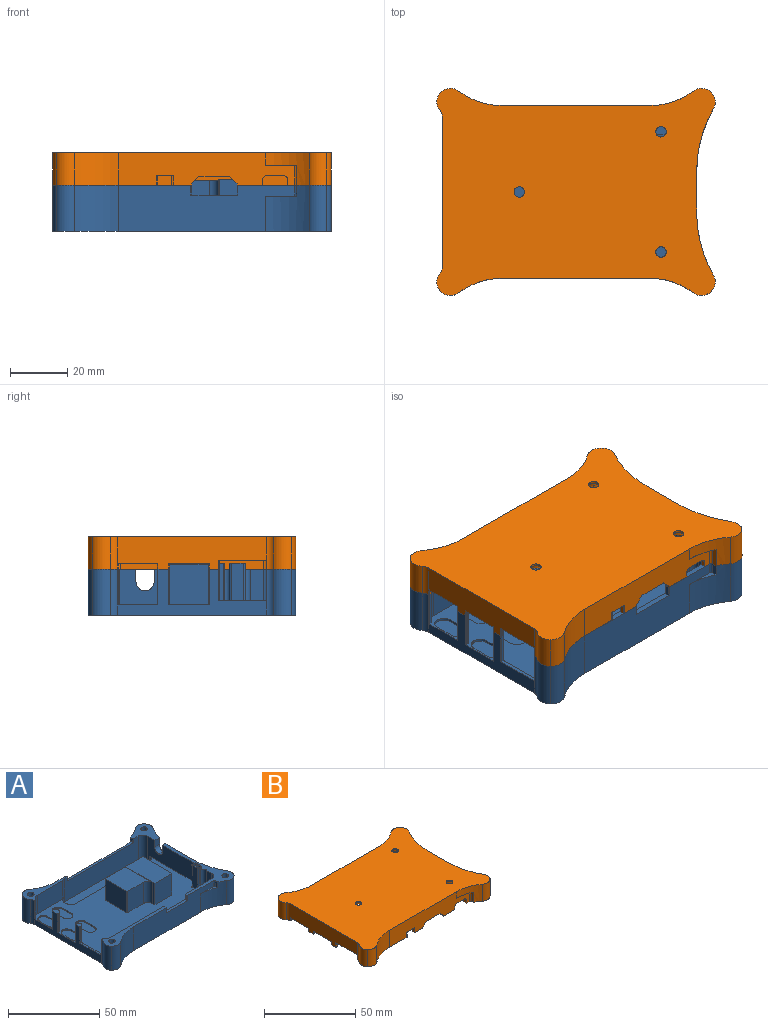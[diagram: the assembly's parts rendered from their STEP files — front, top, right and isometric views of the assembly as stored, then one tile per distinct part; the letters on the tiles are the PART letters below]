
ASSEMBLY  parts=2 mates=1
PART A: 184 faces, bbox 97.3x72.4x18.3 mm
  f0: plane 87x56.52mm, normal (0,0,1), area 3437.9mm2, adj f1,f10,f11,f12,f13,f14,f15,f16
  f1: plane 13.85x1.52mm, normal (1,0,0), area 21.1mm2, adj f0,f59,f88,f141,f172
  f2: plane 20.54x16.18mm, normal (0,0,1), area 276.9mm2, adj f108,f109,f110,f111,f112,f113,f114,f159
  f3: cylinder r=1.83mm len=13.48mm, axis (0,0,-1), area 154.9mm2, adj f62,f157
  f4: cylinder r=1.09mm len=18.29mm, axis (0,0,-1), area 125.5mm2, adj f5,f6
  f5: plane 5.71x3.11mm, normal (0,0,1), area 8.8mm2, adj f4,f7,f8,f9,f10,f11,f12,f13
  f6: plane 97.31x72.42mm, normal (0,0,-1), area 5503.1mm2, adj f4,f19,f20,f21,f22,f23,f24,f25
  f7: cylinder r=0.13mm len=2.21mm, axis (0,0,1), area 0.5mm2, adj f5,f8,f18,f155
  f8: plane 4.33x2.21mm, normal (1,0,0), area 9.6mm2, adj f5,f7,f9,f155
  f9: cylinder r=0.13mm len=2.21mm, axis (0,0,1), area 0.5mm2, adj f5,f8,f10,f155
  f10: cylinder r=1.65mm len=14.66mm, axis (0,0,1), area 62.4mm2, adj f0,f5,f9,f11,f155,f156
  f11: cylinder r=0.13mm len=14.66mm, axis (0,0,1), area 1.5mm2, adj f0,f5,f10,f12
  f12: plane 14.66x0.82mm, normal (0,1,0), area 12mm2, adj f0,f5,f11,f13
  f13: cylinder r=0.79mm len=14.66mm, axis (0,0,1), area 18.3mm2, adj f0,f5,f12,f14
  f14: plane 14.66x4.13mm, normal (-1,0,0), area 60.5mm2, adj f0,f5,f13,f15
  f15: cylinder r=0.79mm len=14.66mm, axis (0,0,1), area 18.3mm2, adj f0,f5,f14,f16
  f16: plane 14.66x0.82mm, normal (0,-1,0), area 12mm2, adj f0,f5,f15,f17
  f17: cylinder r=0.13mm len=14.66mm, axis (0,0,1), area 1.5mm2, adj f0,f5,f16,f18
  f18: cylinder r=1.65mm len=14.66mm, axis (0,0,1), area 62.4mm2, adj f0,f5,f7,f17,f153,f155
  f19: cylinder r=1.09mm len=18.29mm, axis (0,0,-1), area 125.5mm2, adj f5,f6
  f20: cylinder r=4.76mm len=16.08mm, axis (0,0,-1), area 112mm2, adj f6,f21,f39,f52
  f21: cylinder r=4.76mm len=16.08mm, axis (0,0,-1), area 112mm2, adj f6,f20,f22,f52
  f22: cylinder r=3.43mm len=16.08mm, axis (0,0,-1), area 39.1mm2, adj f6,f21,f23,f52,f53
  f23: plane 52.18x16.08mm, normal (-1,0,0), area 301.8mm2, adj f0,f6,f22,f24,f54,f55,f56,f57
  f24: cylinder r=3.43mm len=16.08mm, axis (0,0,-1), area 39.2mm2, adj f6,f23,f25,f61,f62
  f25: cylinder r=4.76mm len=16.08mm, axis (0,0,-1), area 112mm2, adj f6,f24,f26,f62
  f26: cylinder r=4.76mm len=16.08mm, axis (0,0,-1), area 112mm2, adj f6,f25,f27,f62
  f27: cylinder r=25.4mm len=16.08mm, axis (0,0,-1), area 262.8mm2, adj f6,f26,f28,f62
  f28: plane 51.56x16.08mm, normal (0,1,0), area 717mm2, adj f6,f27,f29,f62,f64,f177
  f29: cylinder r=25.4mm len=16.08mm, axis (0,0,-1), area 244.4mm2, adj f6,f28,f30,f64,f66,f176
  f30: cylinder r=4.76mm len=16.08mm, axis (0,0,-1), area 104.7mm2, adj f6,f29,f31,f66
  f31: cylinder r=4.76mm len=16.08mm, axis (0,0,-1), area 104.7mm2, adj f6,f30,f32,f66
  f32: cylinder r=44.45mm len=22.05mm, axis (0,0,-1), area 332.5mm2, adj f6,f31,f33,f66,f67,f68,f69,f70
  f33: plane 16.08x14.04mm, normal (1,0,0), area 225.7mm2, adj f6,f32,f34,f155
  f34: cylinder r=44.45mm len=22.05mm, axis (0,0,-1), area 371mm2, adj f6,f33,f35,f155
  f35: cylinder r=4.76mm len=16.08mm, axis (0,0,-1), area 104.7mm2, adj f6,f34,f36,f155
  f36: cylinder r=4.76mm len=16.08mm, axis (0,0,-1), area 104.7mm2, adj f6,f35,f37,f155
  f37: cylinder r=25.4mm len=16.08mm, axis (0,0,-1), area 220.1mm2, adj f6,f36,f38,f71,f72,f155
  f38: plane 61.61x16.08mm, normal (0,-1,0), area 811.4mm2, adj f6,f37,f39,f52,f72,f73,f149,f155
  f39: cylinder r=25.4mm len=16.08mm, axis (0,0,-1), area 262.8mm2, adj f6,f20,f38,f52
  f40: cone r=1.83mm half-angle=41deg, axis (0,0,-1), area 16mm2, adj f6,f41,f43,f74
  f41: cone r=1.83mm half-angle=41deg, axis (0,0,-1), area 16mm2, adj f6,f40,f42,f75
  f42: cone r=1.83mm half-angle=41deg, axis (0,0,-1), area 16mm2, adj f6,f41,f43,f76
  f43: cone r=1.83mm half-angle=41deg, axis (0,0,-1), area 16mm2, adj f6,f40,f42,f77
  f44: cone r=1.83mm half-angle=41deg, axis (0,0,-1), area 16mm2, adj f6,f45,f47,f78
  f45: cone r=1.83mm half-angle=41deg, axis (0,0,-1), area 16mm2, adj f6,f44,f46,f79
  f46: cone r=1.83mm half-angle=41deg, axis (0,0,-1), area 16mm2, adj f6,f45,f47,f80
  f47: cone r=1.83mm half-angle=41deg, axis (0,0,-1), area 16mm2, adj f6,f44,f46,f81
  f48: cone r=1.83mm half-angle=41deg, axis (0,0,-1), area 16mm2, adj f6,f49,f51,f82
  f49: cone r=1.83mm half-angle=41deg, axis (0,0,-1), area 16mm2, adj f6,f48,f50,f83
  f50: cone r=1.83mm half-angle=41deg, axis (0,0,-1), area 16mm2, adj f6,f49,f51,f84
  f51: cone r=1.83mm half-angle=41deg, axis (0,0,-1), area 16mm2, adj f6,f48,f50,f85
  f52: plane 48.5x10.26mm, normal (0,0,1), area 151.3mm2, adj f20,f21,f22,f38,f39,f53,f74,f75
  f53: cylinder r=0.15mm len=10.92mm, axis (0,0,1), area 2.6mm2, adj f22,f52,f59,f138
  f54: plane 3.71x2.63mm, normal (0,0,1), area 7.6mm2, adj f23,f55,f60,f89,f140,f167,f168,f169
  f55: cylinder r=0.25mm len=12.45mm, axis (0,0,-1), area 5mm2, adj f0,f23,f54,f89
  f56: cylinder r=0.25mm len=12.45mm, axis (0,0,-1), area 5mm2, adj f0,f23,f57,f90
  f57: plane 4.29x2.92mm, normal (0,0,1), area 9.5mm2, adj f23,f56,f58,f90,f91,f160,f161,f162
  f58: cylinder r=0.25mm len=12.45mm, axis (0,0,-1), area 5mm2, adj f0,f23,f57,f91
  f59: plane 17.54x2.2mm, normal (0,0,1), area 19.9mm2, adj f1,f23,f53,f60,f138,f139,f140,f141
  f60: cylinder r=0.25mm len=10.92mm, axis (0,0,-1), area 4.4mm2, adj f23,f54,f59,f140
  f61: cylinder r=0.23mm len=12.45mm, axis (0,0,-1), area 4.5mm2, adj f0,f24,f62,f92
  f62: plane 30.58x10.34mm, normal (0,0,1), area 115.3mm2, adj f3,f24,f25,f26,f27,f28,f61,f63
  f63: plane 2.54x0.84mm, normal (1,0,0), area 2.1mm2, adj f62,f64,f177,f180
  f64: plane 51.31x2.37mm, normal (0,0,1), area 70.6mm2, adj f28,f29,f63,f65,f100,f176,f177,f180
  f65: plane 2.54x1.87mm, normal (-1,0,0), area 4.7mm2, adj f64,f66,f176,f183
  f66: plane 16.61x15.91mm, normal (0,0,1), area 127mm2, adj f29,f30,f31,f32,f65,f67,f78,f79
  f67: plane 4.33x3.84mm, normal (0,-1,0), area 16.6mm2, adj f32,f66,f68,f154
  f68: cylinder r=3.17mm len=3.84mm, axis (1,0,0), area 17.1mm2, adj f32,f67,f69,f154
  f69: cylinder r=3.17mm len=3.18mm, axis (1,0,0), area 13.7mm2, adj f32,f68,f70,f154
  f70: plane 4.33x2.46mm, normal (0,1,0), area 10.7mm2, adj f32,f69,f154,f155
  f71: plane 3.81x1.63mm, normal (-1,0,0), area 6.2mm2, adj f37,f72,f73,f155
  f72: plane 10.87x2.46mm, normal (0,0,1), area 8.5mm2, adj f37,f38,f71,f73
  f73: cylinder r=0.79mm len=3.81mm, axis (0,0,-1), area 4.8mm2, adj f38,f71,f72,f155
  f74: cylinder r=1.83mm len=13.48mm, axis (0,0,-1), area 38.7mm2, adj f40,f52,f75,f77
  f75: cylinder r=1.83mm len=13.48mm, axis (0,0,-1), area 38.7mm2, adj f41,f52,f74,f76
  f76: cylinder r=1.83mm len=13.48mm, axis (0,0,-1), area 38.7mm2, adj f42,f52,f75,f77
  f77: cylinder r=1.83mm len=13.48mm, axis (0,0,-1), area 38.7mm2, adj f43,f52,f74,f76
  f78: cylinder r=1.83mm len=13.48mm, axis (0,0,-1), area 38.7mm2, adj f44,f66,f79,f81
  f79: cylinder r=1.83mm len=13.48mm, axis (0,0,-1), area 38.7mm2, adj f45,f66,f78,f80
  f80: cylinder r=1.83mm len=13.48mm, axis (0,0,-1), area 38.7mm2, adj f46,f66,f79,f81
  f81: cylinder r=1.83mm len=13.48mm, axis (0,0,-1), area 38.7mm2, adj f47,f66,f78,f80
  f82: cylinder r=1.83mm len=13.48mm, axis (0,0,-1), area 38.7mm2, adj f48,f83,f85,f155
  f83: cylinder r=1.83mm len=13.48mm, axis (0,0,-1), area 38.7mm2, adj f49,f82,f84,f155
  f84: cylinder r=1.83mm len=13.48mm, axis (0,0,-1), area 38.7mm2, adj f50,f83,f85,f155
  f85: cylinder r=1.83mm len=13.48mm, axis (0,0,-1), area 38.7mm2, adj f51,f82,f84,f155
  f86: plane 78.74x12.45mm, normal (0,1,0), area 924.1mm2, adj f0,f52,f87,f88,f149,f155,f181,f182
  f87: cylinder r=3.43mm len=12.45mm, axis (0,0,1), area 67mm2, adj f0,f86,f152,f155
  f88: cylinder r=3.43mm len=12.45mm, axis (0,0,-1), area 52.5mm2, adj f0,f1,f52,f86,f139,f141
  f89: plane 12.45x0.83mm, normal (0,1,0), area 10.4mm2, adj f0,f54,f55,f173
  f90: plane 12.45x0.83mm, normal (0,-1,0), area 10.4mm2, adj f0,f56,f57,f165
  f91: plane 12.45x0.83mm, normal (0,1,0), area 10.4mm2, adj f0,f57,f58,f166
  f92: plane 12.45x0.96mm, normal (0,-1,0), area 11.9mm2, adj f0,f61,f62,f93
  f93: cylinder r=0.23mm len=12.45mm, axis (0,0,-1), area 3.5mm2, adj f0,f62,f92,f94
  f94: cylinder r=3.43mm len=12.45mm, axis (0,0,-1), area 52.1mm2, adj f0,f62,f93,f95
  f95: plane 19.81x12.45mm, normal (0,-1,0), area 246.5mm2, adj f0,f62,f94,f142
  f96: cylinder r=3.43mm len=3.07mm, axis (0,0,-1), area 10.4mm2, adj f0,f97,f143,f144
  f97: plane 3.07x1.78mm, normal (1,0,0), area 5.5mm2, adj f0,f96,f98,f143
  f98: cylinder r=3.43mm len=3.43mm, axis (0,0,-1), area 16.6mm2, adj f0,f97,f99,f143
  f99: plane 57.06x3.07mm, normal (0,1,0), area 175.4mm2, adj f0,f98,f143,f175
  f100: plane 57.06x15.52mm, normal (0,-1,0), area 755.2mm2, adj f62,f64,f66,f101,f142,f143,f144,f180
  f101: cylinder r=3.43mm len=15.52mm, axis (0,0,-1), area 83.6mm2, adj f66,f100,f143,f154
  f102: cylinder r=3.17mm len=3.18mm, axis (0,0,-1), area 3.8mm2, adj f0,f103,f107,f145
  f103: plane 6.86x0.76mm, normal (1,0,0), area 5.2mm2, adj f0,f102,f104,f145
  f104: cylinder r=3.17mm len=3.18mm, axis (0,0,-1), area 3.8mm2, adj f0,f103,f105,f145
  f105: cylinder r=3.17mm len=3.18mm, axis (0,0,-1), area 3.8mm2, adj f0,f104,f106,f145
  f106: plane 6.86x0.76mm, normal (-1,0,0), area 5.2mm2, adj f0,f105,f107,f145
  f107: cylinder r=3.17mm len=3.18mm, axis (0,0,-1), area 3.8mm2, adj f0,f102,f106,f145
  f108: plane 28.95x14.4mm, normal (0,1,0), area 414.9mm2, adj f0,f2,f109,f119,f158,f159
  f109: cylinder r=0.25mm len=14.28mm, axis (0,0,-1), area 5.7mm2, adj f0,f2,f108,f110
  f110: plane 16.73x14.28mm, normal (-1,0,0), area 238.8mm2, adj f0,f2,f109,f111
  f111: cylinder r=0.25mm len=14.28mm, axis (0,0,-1), area 5.7mm2, adj f0,f2,f110,f112
  f112: plane 14.28x12.37mm, normal (0,-1,0), area 176.6mm2, adj f0,f2,f111,f113
  f113: cylinder r=3.3mm len=14.28mm, axis (0,0,-1), area 74mm2, adj f0,f2,f112,f114
  f114: plane 22.08x14.4mm, normal (-1,0,0), area 28.4mm2, adj f0,f2,f113,f115,f158,f159
  f115: cylinder r=0.25mm len=14.4mm, axis (0,0,-1), area 5.7mm2, adj f0,f114,f116,f158
  f116: plane 14.4x13.03mm, normal (0,-1,0), area 187.6mm2, adj f0,f115,f117,f158
  f117: cylinder r=0.25mm len=14.4mm, axis (0,0,-1), area 5.7mm2, adj f0,f116,f118,f158
  f118: plane 22.09x14.4mm, normal (1,0,0), area 318.2mm2, adj f0,f117,f119,f158
  f119: cylinder r=0.25mm len=14.4mm, axis (0,0,-1), area 5.6mm2, adj f0,f108,f118,f158
  f120: cylinder r=3.17mm len=3.18mm, axis (0,0,-1), area 3.8mm2, adj f0,f121,f125,f146
  f121: cylinder r=3.17mm len=3.18mm, axis (0,0,-1), area 3.8mm2, adj f0,f120,f122,f146
  f122: plane 6.99x0.76mm, normal (-1,0,0), area 5.3mm2, adj f0,f121,f123,f146
  f123: cylinder r=3.17mm len=3.18mm, axis (0,0,-1), area 3.8mm2, adj f0,f122,f124,f146
  f124: cylinder r=3.17mm len=3.18mm, axis (0,0,-1), area 3.8mm2, adj f0,f123,f125,f146
  f125: plane 6.99x0.76mm, normal (1,0,0), area 5.3mm2, adj f0,f120,f124,f146
  f126: plane 6.99x0.76mm, normal (-1,0,0), area 5.3mm2, adj f0,f127,f131,f147
  f127: cylinder r=3.17mm len=3.18mm, axis (0,0,-1), area 3.8mm2, adj f0,f126,f128,f147
  f128: cylinder r=3.17mm len=3.18mm, axis (0,0,-1), area 3.8mm2, adj f0,f127,f129,f147
  f129: plane 6.99x0.76mm, normal (1,0,0), area 5.3mm2, adj f0,f128,f130,f147
  f130: cylinder r=3.17mm len=3.18mm, axis (0,0,-1), area 3.8mm2, adj f0,f129,f131,f147
  f131: cylinder r=3.17mm len=3.18mm, axis (0,0,-1), area 3.8mm2, adj f0,f126,f130,f147
  f132: cylinder r=3.17mm len=3.18mm, axis (0,0,-1), area 3.8mm2, adj f0,f133,f137,f148
  f133: cylinder r=3.17mm len=3.18mm, axis (0,0,-1), area 3.8mm2, adj f0,f132,f134,f148
  f134: plane 6.86x0.76mm, normal (1,0,0), area 5.2mm2, adj f0,f133,f135,f148
  f135: cylinder r=3.17mm len=3.18mm, axis (0,0,-1), area 3.8mm2, adj f0,f134,f136,f148
  f136: cylinder r=3.17mm len=3.18mm, axis (0,0,-1), area 3.8mm2, adj f0,f135,f137,f148
  f137: plane 6.86x0.76mm, normal (-1,0,0), area 5.2mm2, adj f0,f132,f136,f148
  f138: plane 10.92x1.07mm, normal (0,1,0), area 11.7mm2, adj f52,f53,f59,f139
  f139: cylinder r=0.23mm len=10.92mm, axis (0,0,-1), area 3mm2, adj f52,f59,f88,f138
  f140: plane 10.92x0.83mm, normal (0,-1,0), area 9.1mm2, adj f54,f59,f60,f174
  f141: cylinder r=3.43mm len=1.26mm, axis (0,0,1), area 0.4mm2, adj f1,f59,f88
  f142: cylinder r=3.43mm len=12.45mm, axis (0,0,-1), area 24.7mm2, adj f62,f95,f100,f144
  f143: plane 63.91x8.64mm, normal (0,0,1), area 541.9mm2, adj f96,f97,f98,f99,f100,f101,f144,f154
  f144: cylinder r=3.43mm len=3.07mm, axis (0,0,-1), area 6.1mm2, adj f96,f100,f142,f143
  f145: plane 13.21x6.35mm, normal (0,0,1), area 75.2mm2, adj f102,f103,f104,f105,f106,f107
  f146: plane 13.34x6.35mm, normal (0,0,1), area 76mm2, adj f120,f121,f122,f123,f124,f125
  f147: plane 13.34x6.35mm, normal (0,0,1), area 76mm2, adj f126,f127,f128,f129,f130,f131
  f148: plane 13.21x6.35mm, normal (0,0,1), area 75.2mm2, adj f132,f133,f134,f135,f136,f137
  f149: plane 16.38x1.91mm, normal (0,0,1), area 30.3mm2, adj f38,f86,f150,f151,f178,f179,f181,f182
  f150: plane 3.41x1.4mm, normal (1,0,0), area 4.8mm2, adj f52,f149,f179,f181
  f151: plane 3.41x1.4mm, normal (-1,0,0), area 4.8mm2, adj f149,f155,f178,f182
  f152: plane 12.45x4.23mm, normal (-1,0,0), area 52.6mm2, adj f0,f87,f153,f155
  f153: cylinder r=0.13mm len=12.45mm, axis (0,0,1), area 0.8mm2, adj f0,f18,f152,f155
  f154: plane 36.43x15.52mm, normal (-1,0,0), area 415.6mm2, adj f0,f66,f67,f68,f69,f70,f101,f143
  f155: plane 49.43x32.91mm, normal (0,0,1), area 238.2mm2, adj f7,f8,f9,f10,f18,f32,f33,f34
  f156: cylinder r=0.13mm len=12.45mm, axis (0,0,1), area 0.8mm2, adj f0,f10,f154,f155
  f157: cone r=1.83mm half-angle=41deg, axis (0,0,-1), area 64.1mm2, adj f3,f6
  f158: plane 22.59x13.53mm, normal (0,0,1), area 305.7mm2, adj f108,f114,f115,f116,f117,f118,f119,f159
  f159: cylinder r=0.25mm len=0.25mm, axis (0,0,-1), area 0.1mm2, adj f2,f108,f114,f158
  f160: plane 12.45x1.57mm, normal (0.71,-0.71,0), area 27.6mm2, adj f0,f57,f161,f165
  f161: cylinder r=0.25mm len=12.45mm, axis (0,0,1), area 2.5mm2, adj f0,f57,f160,f162
  f162: plane 12.45x0.64mm, normal (1,0,0), area 7.9mm2, adj f0,f57,f161,f163
  f163: cylinder r=0.25mm len=12.45mm, axis (0,0,1), area 2.5mm2, adj f0,f57,f162,f164
  f164: plane 12.45x1.57mm, normal (0.71,0.71,0), area 27.6mm2, adj f0,f57,f163,f166
  f165: cylinder r=0.25mm len=12.45mm, axis (0,0,-1), area 2.5mm2, adj f0,f57,f90,f160
  f166: cylinder r=0.25mm len=12.45mm, axis (0,0,-1), area 2.5mm2, adj f0,f57,f91,f164
  f167: plane 12.45x1.28mm, normal (0.71,-0.71,0), area 20.5mm2, adj f0,f54,f59,f168,f172,f174
  f168: cylinder r=0.25mm len=12.45mm, axis (0,0,1), area 2.5mm2, adj f0,f54,f167,f169
  f169: plane 12.45x0.64mm, normal (1,0,0), area 7.9mm2, adj f0,f54,f168,f170
  f170: cylinder r=0.25mm len=12.45mm, axis (0,0,1), area 2.5mm2, adj f0,f54,f169,f171
  f171: plane 12.45x1.28mm, normal (0.71,0.71,0), area 22.5mm2, adj f0,f54,f170,f173
  f172: cylinder r=3.43mm len=2.42mm, axis (0,0,1), area 4.1mm2, adj f0,f1,f59,f167
  f173: cylinder r=0.25mm len=12.45mm, axis (0,0,-1), area 2.5mm2, adj f0,f54,f89,f171
  f174: cylinder r=0.25mm len=10.92mm, axis (0,0,-1), area 2.2mm2, adj f54,f59,f140,f167
  f175: cylinder r=3.43mm len=3.43mm, axis (0,0,1), area 16.6mm2, adj f0,f99,f143,f154
  f176: cylinder r=0.25mm len=2.54mm, axis (0,0,-1), area 0.8mm2, adj f29,f64,f65,f66
  f177: cylinder r=0.25mm len=2.54mm, axis (0,0,1), area 1mm2, adj f28,f62,f63,f64
  f178: cylinder r=0.25mm len=3.41mm, axis (0,0,-1), area 1.4mm2, adj f38,f149,f151,f155
  f179: cylinder r=0.25mm len=3.41mm, axis (0,0,1), area 1.4mm2, adj f38,f52,f149,f150
  f180: cylinder r=0.25mm len=2.54mm, axis (0,0,-1), area 1mm2, adj f62,f63,f64,f100
  f181: cylinder r=0.25mm len=3.41mm, axis (0,0,-1), area 1.4mm2, adj f52,f86,f149,f150
  f182: cylinder r=0.25mm len=3.41mm, axis (0,0,1), area 1.4mm2, adj f86,f149,f151,f155
  f183: cylinder r=0.25mm len=2.54mm, axis (0,0,-1), area 1mm2, adj f64,f65,f66,f100
PART B: 145 faces, bbox 97.3x72.4x11.5 mm
  f0: cylinder r=1.83mm len=3.66mm, axis (0,0,1), area 9mm2, adj f73,f140
  f1: plane 41.64x8.05mm, normal (0,-1,0), area 335.3mm2, adj f2,f11,f17,f63,f139
  f2: plane 97.28x72.39mm, normal (0,0,-1), area 561.9mm2, adj f1,f3,f13,f16,f17,f18,f19,f20
  f3: plane 78.79x8.05mm, normal (0,1,0), area 540.5mm2, adj f2,f4,f6,f8,f9,f10,f11,f12
  f4: plane 6.49x1.91mm, normal (0,0,-1), area 12.3mm2, adj f3,f5,f116,f124,f143,f144
  f5: plane 3.43x1.4mm, normal (-1,0,0), area 4.8mm2, adj f4,f6,f143,f144
  f6: plane 5.99x1.91mm, normal (0,0,-1), area 10.5mm2, adj f3,f5,f7,f124,f141,f142,f143,f144
  f7: plane 3.43x1.4mm, normal (1,0,0), area 4.8mm2, adj f6,f8,f141,f142
  f8: plane 36.55x10.28mm, normal (0,0,-1), area 131.5mm2, adj f3,f7,f9,f49,f50,f51,f52,f53
  f9: cylinder r=3.43mm len=7.95mm, axis (0,0,-1), area 38.6mm2, adj f3,f8,f10,f55,f60,f61
  f10: cylinder r=3.43mm len=3.43mm, axis (0,0,-1), area 0.5mm2, adj f3,f9,f11,f61
  f11: plane 85.65x57.4mm, normal (0,0,-1), area 4380.3mm2, adj f1,f3,f10,f12,f16,f18,f61,f62
  f12: cylinder r=3.43mm len=3.43mm, axis (0,0,-1), area 0.5mm2, adj f3,f11,f13,f16
  f13: cylinder r=3.43mm len=7.95mm, axis (0,0,-1), area 42.8mm2, adj f2,f3,f12,f16
  f14: plane 1.91x1.83mm, normal (1,0,0), area 3.5mm2, adj f3,f15,f117,f124
  f15: plane 8.9x1.91mm, normal (0,0,-1), area 17mm2, adj f3,f14,f115,f124
  f16: plane 49.66x8.05mm, normal (-1,0,0), area 399.8mm2, adj f2,f11,f12,f13,f17,f63
  f17: cylinder r=3.43mm len=7.95mm, axis (0,0,-1), area 42.8mm2, adj f1,f2,f16,f63
  f18: plane 21.27x8.05mm, normal (0,-1,0), area 171.3mm2, adj f2,f11,f19,f62,f138
  f19: cylinder r=3.43mm len=7.95mm, axis (0,0,-1), area 40.4mm2, adj f2,f18,f20,f61,f62,f72
  f20: cylinder r=0.23mm len=2.03mm, axis (0,0,-1), area 0.6mm2, adj f2,f19,f21,f72
  f21: plane 2.03x0.91mm, normal (0,-1,0), area 1.8mm2, adj f2,f20,f22,f72
  f22: cylinder r=0.23mm len=2.03mm, axis (0,0,-1), area 0.7mm2, adj f2,f21,f23,f72
  f23: cylinder r=3.43mm len=11.43mm, axis (0,0,-1), area 27.8mm2, adj f2,f22,f24,f73,f74
  f24: cylinder r=4.76mm len=11.43mm, axis (0,0,-1), area 79.6mm2, adj f2,f23,f25,f73
  f25: cylinder r=4.76mm len=11.43mm, axis (0,0,-1), area 79.6mm2, adj f2,f24,f26,f73
  f26: cylinder r=25.4mm len=15.24mm, axis (0,0,-1), area 186.8mm2, adj f2,f25,f27,f73
  f27: plane 51.56x11.43mm, normal (0,1,0), area 589.4mm2, adj f2,f26,f28,f73
  f28: cylinder r=25.4mm len=15.24mm, axis (0,0,-1), area 186.8mm2, adj f2,f27,f29,f73
  f29: cylinder r=4.76mm len=11.43mm, axis (0,0,-1), area 74.4mm2, adj f2,f28,f30,f73
  f30: cylinder r=4.76mm len=11.43mm, axis (0,0,-1), area 74.4mm2, adj f2,f29,f31,f73
  f31: cylinder r=44.45mm len=22.05mm, axis (0,0,-1), area 263.7mm2, adj f2,f30,f32,f73
  f32: plane 14.04x11.43mm, normal (1,0,0), area 160.4mm2, adj f2,f31,f33,f73
  f33: cylinder r=44.45mm len=22.05mm, axis (0,0,-1), area 263.7mm2, adj f2,f32,f34,f73
  f34: cylinder r=4.76mm len=11.43mm, axis (0,0,-1), area 74.4mm2, adj f2,f33,f35,f73
  f35: cylinder r=4.76mm len=11.43mm, axis (0,0,-1), area 74.4mm2, adj f2,f34,f36,f73
  f36: cylinder r=25.4mm len=15.24mm, axis (0,0,-1), area 108.6mm2, adj f2,f35,f73,f119,f123,f124
  f37: cylinder r=1.52mm len=9.88mm, axis (0,0,-1), area 23.6mm2, adj f2,f38,f40,f75
  f38: cylinder r=1.52mm len=9.88mm, axis (0,0,-1), area 23.6mm2, adj f2,f37,f39,f76
  f39: cylinder r=1.52mm len=9.88mm, axis (0,0,-1), area 23.6mm2, adj f2,f38,f40,f77
  f40: cylinder r=1.52mm len=9.88mm, axis (0,0,-1), area 23.6mm2, adj f2,f37,f39,f78
  f41: cylinder r=1.52mm len=9.88mm, axis (0,0,-1), area 23.6mm2, adj f2,f42,f44,f79
  f42: cylinder r=1.52mm len=9.88mm, axis (0,0,-1), area 23.6mm2, adj f2,f41,f43,f80
  f43: cylinder r=1.52mm len=9.88mm, axis (0,0,-1), area 23.6mm2, adj f2,f42,f44,f81
  f44: cylinder r=1.52mm len=9.88mm, axis (0,0,-1), area 23.6mm2, adj f2,f41,f43,f82
  f45: cylinder r=1.52mm len=9.88mm, axis (0,0,-1), area 23.6mm2, adj f2,f46,f48,f83
  f46: cylinder r=1.52mm len=9.88mm, axis (0,0,-1), area 23.6mm2, adj f2,f45,f47,f84
  f47: cylinder r=1.52mm len=9.88mm, axis (0,0,-1), area 23.6mm2, adj f2,f46,f48,f85
  f48: cylinder r=1.52mm len=9.88mm, axis (0,0,-1), area 23.6mm2, adj f2,f45,f47,f86
  f49: cylinder r=25.4mm len=15.24mm, axis (0,0,-1), area 186.8mm2, adj f8,f50,f73,f124
  f50: cylinder r=4.76mm len=11.43mm, axis (0,0,-1), area 79.6mm2, adj f8,f49,f51,f73
  f51: cylinder r=4.76mm len=11.43mm, axis (0,0,-1), area 79.6mm2, adj f8,f50,f52,f73
  f52: cylinder r=3.43mm len=11.43mm, axis (0,0,-1), area 27.5mm2, adj f8,f51,f53,f60,f73,f74
  f53: cylinder r=0.25mm len=3.23mm, axis (0,0,-1), area 1.3mm2, adj f8,f52,f54,f60
  f54: plane 3.23x0.9mm, normal (0,1,0), area 2.9mm2, adj f8,f53,f55,f60
  f55: cylinder r=0.25mm len=3.23mm, axis (0,0,-1), area 1mm2, adj f8,f9,f54,f60
  f56: cylinder r=1.52mm len=9.88mm, axis (0,0,-1), area 23.6mm2, adj f8,f57,f59,f87
  f57: cylinder r=1.52mm len=9.88mm, axis (0,0,-1), area 23.6mm2, adj f8,f56,f58,f88
  f58: cylinder r=1.52mm len=9.88mm, axis (0,0,-1), area 23.6mm2, adj f8,f57,f59,f89
  f59: cylinder r=1.52mm len=9.88mm, axis (0,0,-1), area 23.6mm2, adj f8,f56,f58,f90
  f60: plane 16.89x1.39mm, normal (0,0,-1), area 18.8mm2, adj f9,f52,f53,f54,f55,f61,f74,f91
  f61: plane 49.66x8.05mm, normal (1,0,0), area 294.6mm2, adj f9,f10,f11,f19,f60,f62,f72,f93
  f62: cylinder r=3.43mm len=3.43mm, axis (0,0,-1), area 0.5mm2, adj f11,f18,f19,f61
  f63: cylinder r=3.43mm len=3.43mm, axis (0,0,-1), area 0.5mm2, adj f1,f11,f16,f17
  f64: cone r=1.83mm half-angle=41deg, axis (0,0,-1), area 16mm2, adj f11,f65,f67,f100
  f65: cone r=1.83mm half-angle=41deg, axis (0,0,-1), area 16mm2, adj f11,f64,f66,f101
  f66: cone r=1.83mm half-angle=41deg, axis (0,0,-1), area 16mm2, adj f11,f65,f67,f102
  f67: cone r=1.83mm half-angle=41deg, axis (0,0,-1), area 16mm2, adj f11,f64,f66,f103
  f68: cone r=1.83mm half-angle=41deg, axis (0,0,-1), area 16mm2, adj f11,f69,f71,f104
  f69: cone r=1.83mm half-angle=41deg, axis (0,0,-1), area 16mm2, adj f11,f68,f70,f105
  f70: cone r=1.83mm half-angle=41deg, axis (0,0,-1), area 16mm2, adj f11,f69,f71,f106
  f71: cone r=1.83mm half-angle=41deg, axis (0,0,-1), area 16mm2, adj f11,f68,f70,f107
  f72: plane 14.21x1.36mm, normal (0,0,-1), area 15.8mm2, adj f19,f20,f21,f22,f61,f74,f94,f108
  f73: plane 97.28x72.39mm, normal (0,0,1), area 5689.1mm2, adj f0,f23,f24,f25,f26,f27,f28,f29
  f74: plane 52.18x11.43mm, normal (-1,0,0), area 484.5mm2, adj f23,f52,f60,f72,f73,f91,f95,f97
  f75: cone r=0.8mm half-angle=59deg, axis (0,0,-1), area 2.1mm2, adj f37,f76,f78
  f76: cone r=0.8mm half-angle=59deg, axis (0,0,-1), area 2.1mm2, adj f38,f75,f77
  f77: cone r=0.8mm half-angle=59deg, axis (0,0,-1), area 2.1mm2, adj f39,f76,f78
  f78: cone r=0.8mm half-angle=59deg, axis (0,0,-1), area 2.1mm2, adj f40,f75,f77
  f79: cone r=0.8mm half-angle=59deg, axis (0,0,-1), area 2.1mm2, adj f41,f80,f82
  f80: cone r=0.8mm half-angle=59deg, axis (0,0,-1), area 2.1mm2, adj f42,f79,f81
  f81: cone r=0.8mm half-angle=59deg, axis (0,0,-1), area 2.1mm2, adj f43,f80,f82
  f82: cone r=0.8mm half-angle=59deg, axis (0,0,-1), area 2.1mm2, adj f44,f79,f81
  f83: cone r=0.8mm half-angle=59deg, axis (0,0,-1), area 2.1mm2, adj f45,f84,f86
  f84: cone r=0.8mm half-angle=59deg, axis (0,0,-1), area 2.1mm2, adj f46,f83,f85
  f85: cone r=0.8mm half-angle=59deg, axis (0,0,-1), area 2.1mm2, adj f47,f84,f86
  f86: cone r=0.8mm half-angle=59deg, axis (0,0,-1), area 2.1mm2, adj f48,f83,f85
  f87: cone r=0.8mm half-angle=59deg, axis (0,0,-1), area 2.1mm2, adj f56,f88,f90
  f88: cone r=0.8mm half-angle=59deg, axis (0,0,-1), area 2.1mm2, adj f57,f87,f89
  f89: cone r=0.8mm half-angle=59deg, axis (0,0,-1), area 2.1mm2, adj f58,f88,f90
  f90: cone r=0.8mm half-angle=59deg, axis (0,0,-1), area 2.1mm2, adj f59,f87,f89
  f91: cylinder r=0.25mm len=3.23mm, axis (0,0,-1), area 1.3mm2, adj f60,f74,f92,f95
  f92: plane 3.23x0.63mm, normal (0,-1,0), area 2mm2, adj f60,f91,f93,f95
  f93: cylinder r=0.25mm len=3.23mm, axis (0,0,-1), area 1.3mm2, adj f60,f61,f92,f95
  f94: cylinder r=0.25mm len=2.03mm, axis (0,0,1), area 0.8mm2, adj f61,f72,f99,f108
  f95: plane 3.71x1.15mm, normal (0,0,-1), area 4.2mm2, adj f61,f74,f91,f92,f93,f96,f110,f112
  f96: cylinder r=0.25mm len=2.03mm, axis (0,0,-1), area 0.8mm2, adj f61,f95,f97,f112
  f97: plane 14.23x1.15mm, normal (0,0,-1), area 15.7mm2, adj f61,f74,f96,f98,f110,f111,f112,f113
  f98: cylinder r=0.25mm len=2.03mm, axis (0,0,-1), area 0.8mm2, adj f61,f97,f99,f113
  f99: plane 4.29x1.15mm, normal (0,0,-1), area 4.8mm2, adj f61,f74,f94,f98,f108,f109,f111,f113
  f100: cylinder r=1.83mm len=1.83mm, axis (0,0,-1), area 2.2mm2, adj f64,f73,f101,f103
  f101: cylinder r=1.83mm len=1.83mm, axis (0,0,-1), area 2.2mm2, adj f65,f73,f100,f102
  f102: cylinder r=1.83mm len=1.83mm, axis (0,0,-1), area 2.2mm2, adj f66,f73,f101,f103
  f103: cylinder r=1.83mm len=1.83mm, axis (0,0,-1), area 2.2mm2, adj f67,f73,f100,f102
  f104: cylinder r=1.83mm len=1.83mm, axis (0,0,-1), area 2.2mm2, adj f68,f73,f105,f107
  f105: cylinder r=1.83mm len=1.83mm, axis (0,0,-1), area 2.2mm2, adj f69,f73,f104,f106
  f106: cylinder r=1.83mm len=1.83mm, axis (0,0,-1), area 2.2mm2, adj f70,f73,f105,f107
  f107: cylinder r=1.83mm len=1.83mm, axis (0,0,-1), area 2.2mm2, adj f71,f73,f104,f106
  f108: plane 2.03x0.63mm, normal (0,1,0), area 1.3mm2, adj f72,f94,f99,f109
  f109: cylinder r=0.25mm len=2.03mm, axis (0,0,-1), area 0.8mm2, adj f72,f74,f99,f108
  f110: cylinder r=0.25mm len=2.03mm, axis (0,0,-1), area 0.8mm2, adj f74,f95,f97,f112
  f111: cylinder r=0.25mm len=2.03mm, axis (0,0,-1), area 0.8mm2, adj f74,f97,f99,f113
  f112: plane 2.03x0.63mm, normal (0,1,0), area 1.3mm2, adj f95,f96,f97,f110
  f113: plane 2.03x0.63mm, normal (0,-1,0), area 1.3mm2, adj f97,f98,f99,f111
  f114: plane 10.8x1.91mm, normal (0,0,-1), area 20.6mm2, adj f3,f124,f126,f127
  f115: plane 1.91x0.64mm, normal (-1,0,0), area 1.2mm2, adj f3,f15,f124,f126
  f116: plane 1.91x0.64mm, normal (1,0,0), area 1.2mm2, adj f3,f4,f124,f127
  f117: cylinder r=1.6mm len=1.91mm, axis (0,1,0), area 4.8mm2, adj f3,f14,f118,f124
  f118: plane 5.69x1.91mm, normal (0,0,-1), area 10.8mm2, adj f3,f117,f120,f124
  f119: cylinder r=25.4mm len=10.84mm, axis (0,0,-1), area 0.2mm2, adj f36,f122,f124
  f120: cylinder r=1.6mm len=1.91mm, axis (0,1,0), area 4.8mm2, adj f3,f118,f121,f124
  f121: plane 1.91x1.83mm, normal (-1,0,0), area 3.5mm2, adj f2,f3,f120,f124
  f122: plane 10.84x2.43mm, normal (0,0,-1), area 8.5mm2, adj f119,f123,f124,f125
  f123: plane 6.97x1.63mm, normal (-1,0,0), area 11.4mm2, adj f2,f36,f122,f125
  f124: plane 61.61x11.43mm, normal (0,-1,0), area 565.5mm2, adj f2,f4,f6,f8,f14,f15,f36,f49
  f125: cylinder r=0.79mm len=6.97mm, axis (0,0,1), area 8.7mm2, adj f2,f122,f123,f124
  f126: plane 2.54x2.54mm, normal (-0.71,0,-0.71), area 6.8mm2, adj f3,f114,f115,f124
  f127: plane 2.54x2.54mm, normal (0.71,0,-0.71), area 6.8mm2, adj f3,f114,f116,f124
  f128: plane 22.07x3.05mm, normal (-1,0,0), area 67.3mm2, adj f11,f132,f133,f136
  f129: plane 13.03x3.05mm, normal (0,1,0), area 39.7mm2, adj f11,f132,f133,f134
  f130: plane 22.07x3.05mm, normal (1,0,0), area 67.3mm2, adj f11,f132,f134,f135
  f131: plane 13.03x3.05mm, normal (0,-1,0), area 39.7mm2, adj f11,f132,f135,f136
  f132: plane 22.58x13.54mm, normal (0,0,-1), area 305.6mm2, adj f128,f129,f130,f131,f133,f134,f135,f136
  f133: cylinder r=0.25mm len=3.05mm, axis (0,0,-1), area 1.2mm2, adj f11,f128,f129,f132
  f134: cylinder r=0.25mm len=3.05mm, axis (0,0,1), area 1.2mm2, adj f11,f129,f130,f132
  f135: cylinder r=0.25mm len=3.05mm, axis (0,0,-1), area 1.2mm2, adj f11,f130,f131,f132
  f136: cylinder r=0.25mm len=3.05mm, axis (0,0,1), area 1.2mm2, adj f11,f128,f131,f132
  f137: plane 11.27x8.05mm, normal (0,-1,0), area 90.7mm2, adj f2,f11,f138,f139
  f138: cylinder r=3.43mm len=8.05mm, axis (0,0,1), area 20.3mm2, adj f2,f11,f18,f137
  f139: cylinder r=3.43mm len=8.05mm, axis (0,0,1), area 20.3mm2, adj f1,f2,f11,f137
  f140: cone r=1.83mm half-angle=41deg, axis (0,0,-1), area 63.9mm2, adj f0,f11
  f141: cylinder r=0.25mm len=3.43mm, axis (0,0,-1), area 1.4mm2, adj f3,f6,f7,f8
  f142: cylinder r=0.25mm len=3.43mm, axis (0,0,1), area 1.4mm2, adj f6,f7,f8,f124
  f143: cylinder r=0.25mm len=3.43mm, axis (0,0,1), area 1.4mm2, adj f3,f4,f5,f6
  f144: cylinder r=0.25mm len=3.43mm, axis (0,0,-1), area 1.4mm2, adj f4,f5,f6,f124
PLACE A at identity
PLACE B t=(0,0,15.82)mm
MATE fastened B.f87 <-> A.f21  axis (0,0,-1) through (-620.4,-421,16.46)mm
